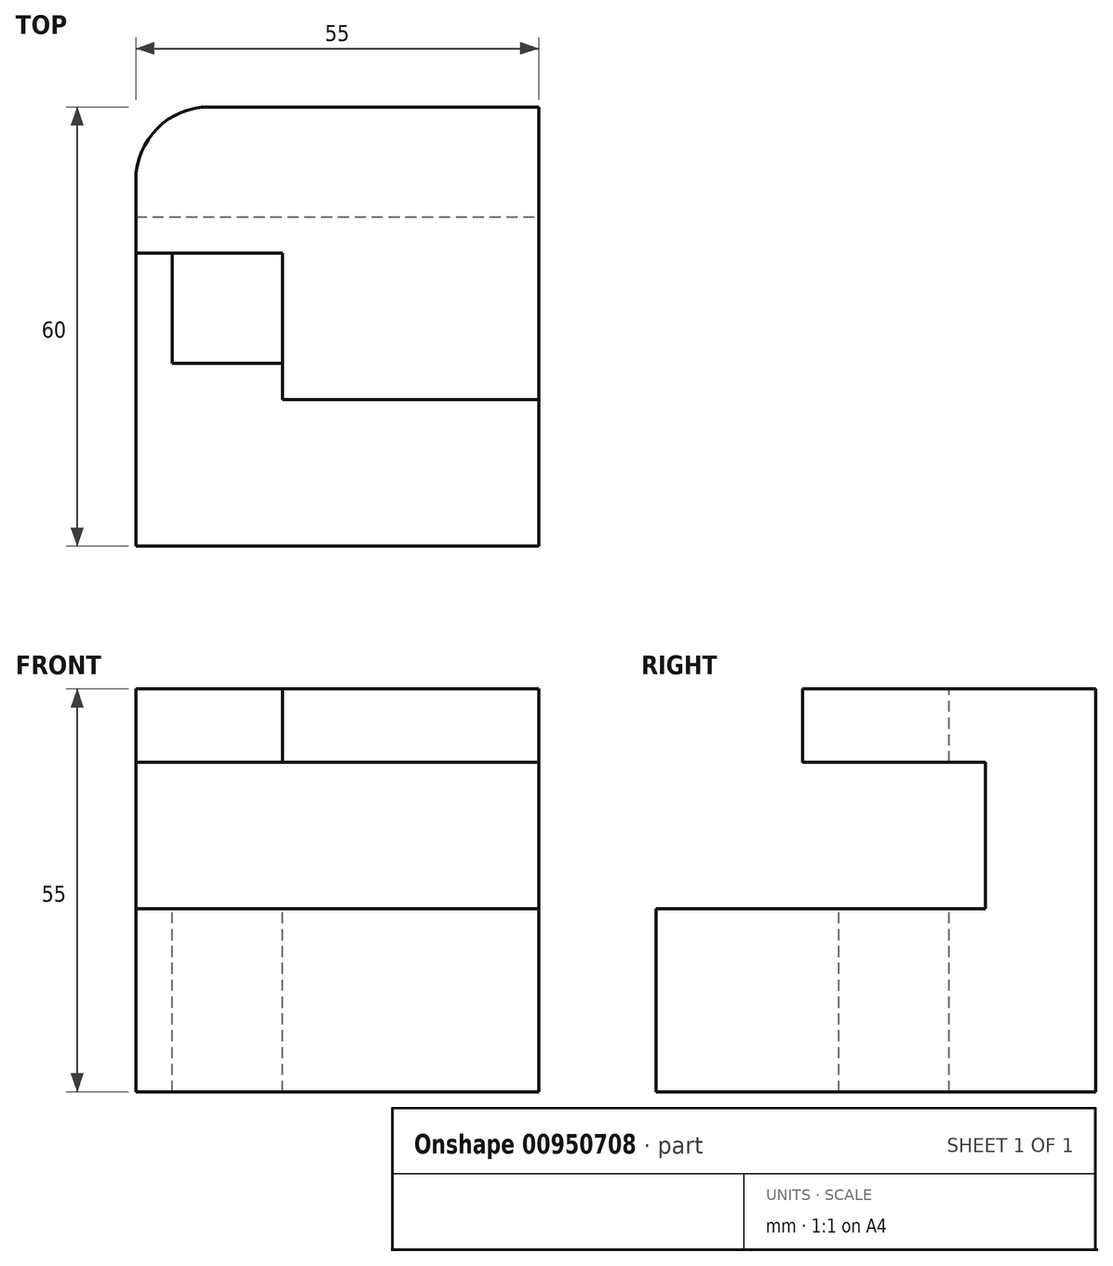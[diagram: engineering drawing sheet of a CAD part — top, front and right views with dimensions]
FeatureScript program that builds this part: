
annotation { "Feature Type Name" : "Feature", "Feature Type Description" : "" }
export const myFeature = defineFeature(function(context is Context, id is Id, definition is map)
    precondition{}
    {
        {
            var Q0;
            Q0=qCreatedBy(makeId("Top.planeOp"),FACE);
            var sketch = newSketch(context, id + "F0", { "sketchPlane" : qUnion([Q0])});
            skLineSegment(sketch, "E0.bottom", {"start": v(0, 0) * mm, "end": v(55, 0) * mm});
            skLineSegment(sketch, "E0.top", {"start": v(0, 60) * mm, "end": v(55, 60) * mm});
            skLineSegment(sketch, "E0.left", {"start": v(0, 0) * mm, "end": v(0, 60) * mm});
            skLineSegment(sketch, "E0.right", {"start": v(55, 0) * mm, "end": v(55, 60) * mm});
            skSolve(sketch);
        }
        {
            var Q0;
            Q0 = qSketchRegion(id + "F0", true);
            extrude(context, id + "F1", {"entities" : qUnion([Q0]), "depth" : 55 * mm, "offsetDistance" : 25 * mm});
        }
        {
            var Q0;
            Q0=makeQuery(id+"F1.opExtrude","SWEPT_FACE",FACE,{"disambiguationData":[OSD([sQuery(id+"F0.wireOp",EDGE,"E0.right")])]});
            var sketch = newSketch(context, id + "F2", { "sketchPlane" : qUnion([Q0])});
            skLineSegment(sketch, "E1", {"start": v(0, 55) * mm, "end": v(20, 55) * mm});
            skLineSegment(sketch, "E2", {"start": v(20, 55) * mm, "end": v(20, 45) * mm});
            skLineSegment(sketch, "E3", {"start": v(20, 45) * mm, "end": v(45, 45) * mm});
            skLineSegment(sketch, "E4", {"start": v(45, 45) * mm, "end": v(45, 25) * mm});
            skLineSegment(sketch, "E5", {"start": v(45, 25) * mm, "end": v(0, 25) * mm});
            skLineSegment(sketch, "E6", {"start": v(0, 25) * mm, "end": v(0, 55) * mm});
            skSolve(sketch);
        }
        {
            var Q0;
            Q0 = qSketchRegion(id + "F2", true);
            extrude(context, id + "F3", {"entities" : qUnion([Q0]), "operationType" : NewBodyOperationType.REMOVE, "endBound" : BoundingType.THROUGH_ALL, "oppositeDirection" : true, "depth" : 25 * mm, "offsetDistance" : 25 * mm});
        }
        {
            var Q0;
            Q0=makeQuery(id+"F1.opExtrude","SWEPT_EDGE",EDGE,{"disambiguationData":[OSD([sQuery(id+"F0.wireOp",EDGE,"E0.top"),sQuery(id+"F0.wireOp",EDGE,"E0.left")])]});
            fillet(context, id + "F4", {"entities" : qUnion([Q0]), "radius" : 10 * mm, "tangentPropagation" : true, "allowEdgeOverflow" : false});
        }
        {
            var Q0;
            Q0=makeQuery(id+"F1.opExtrude","CAP_FACE",FACE,{"disambiguationData":[OSD([sQuery(id+"F0.wireOp",EDGE,"E0.bottom"),sQuery(id+"F0.wireOp",EDGE,"E0.top"),sQuery(id+"F0.wireOp",EDGE,"E0.left"),sQuery(id+"F0.wireOp",EDGE,"E0.right")])],"isStart":false});
            var sketch = newSketch(context, id + "F5", { "sketchPlane" : qUnion([Q0])});
            skLineSegment(sketch, "E7.bottom", {"start": v(20, 20) * mm, "end": v(0, 20) * mm});
            skLineSegment(sketch, "E7.top", {"start": v(20, 40) * mm, "end": v(0, 40) * mm});
            skLineSegment(sketch, "E7.left", {"start": v(20, 20) * mm, "end": v(20, 40) * mm});
            skLineSegment(sketch, "E7.right", {"start": v(0, 20) * mm, "end": v(0, 40) * mm});
            skSolve(sketch);
        }
        {
            var Q0;
            Q0 = qSketchRegion(id + "F5", true);
            extrude(context, id + "F6", {"entities" : qUnion([Q0]), "operationType" : NewBodyOperationType.REMOVE, "endBound" : BoundingType.UP_TO_NEXT, "oppositeDirection" : true, "depth" : 25 * mm, "offsetDistance" : 25 * mm});
        }
        {
            var Q0;
            Q0=makeQuery(id+"F3.boolean.opBoolean","COPY",FACE,{"derivedFrom":makeQuery(id+"F3.opExtrude","SWEPT_FACE",FACE,{"disambiguationData":[OSD([sQuery(id+"F2.wireOp",EDGE,"E5")])]})});
            var sketch = newSketch(context, id + "F7", { "sketchPlane" : qUnion([Q0])});
            skLineSegment(sketch, "E8.bottom", {"start": v(20, 40) * mm, "end": v(5, 40) * mm});
            skLineSegment(sketch, "E8.top", {"start": v(20, 25) * mm, "end": v(5, 25) * mm});
            skLineSegment(sketch, "E8.left", {"start": v(20, 40) * mm, "end": v(20, 25) * mm});
            skLineSegment(sketch, "E8.right", {"start": v(5, 40) * mm, "end": v(5, 25) * mm});
            skSolve(sketch);
        }
        {
            var Q0;
            Q0 = qSketchRegion(id + "F7", true);
            extrude(context, id + "F8", {"entities" : qUnion([Q0]), "operationType" : NewBodyOperationType.REMOVE, "endBound" : BoundingType.THROUGH_ALL, "oppositeDirection" : true, "depth" : 25 * mm, "offsetDistance" : 25 * mm});
        }
    });
